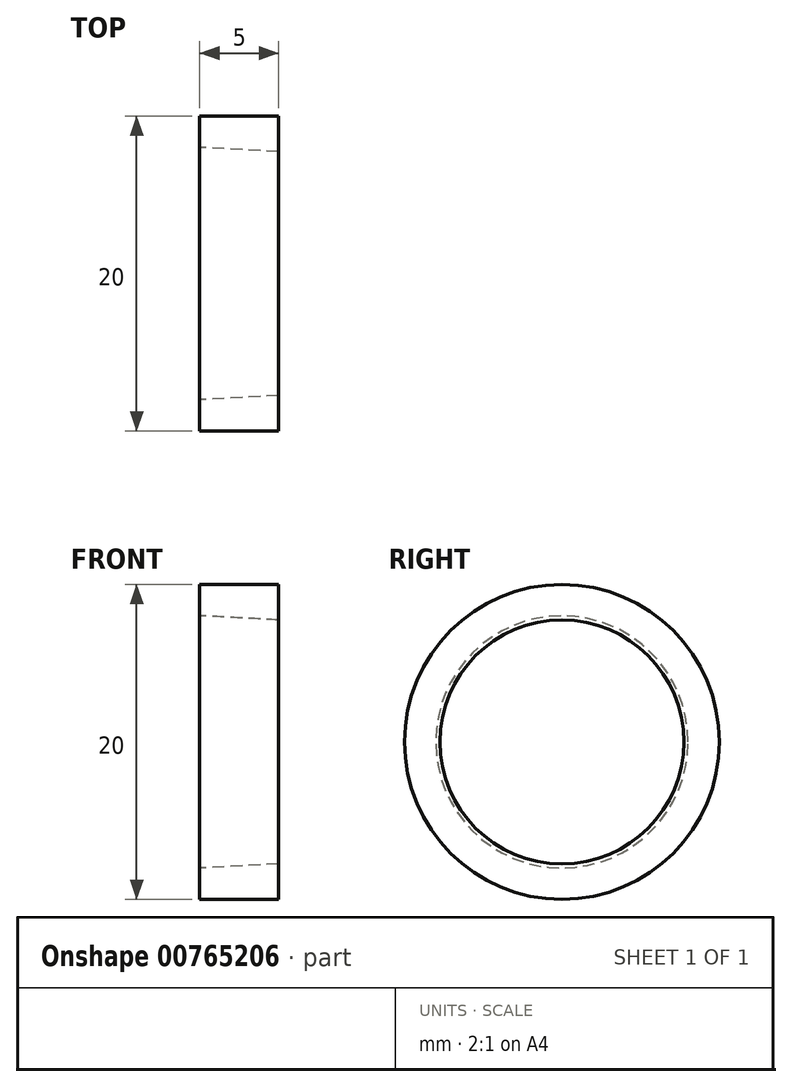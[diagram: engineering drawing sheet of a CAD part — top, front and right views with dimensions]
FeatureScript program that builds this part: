
annotation { "Feature Type Name" : "Feature", "Feature Type Description" : "" }
export const myFeature = defineFeature(function(context is Context, id is Id, definition is map)
    precondition{}
    {
        {
            var Q0;
            Q0=qCreatedBy(makeId("Front.planeOp"),FACE);
            var sketch = newSketch(context, id + "F0", { "sketchPlane" : qUnion([Q0])});
            skLineSegment(sketch, "E0", {"start": v(0, 10) * mm, "end": v(5, 10) * mm});
            skLineSegment(sketch, "E1", {"start": v(5, 7.75) * mm, "end": v(0, 8.01) * mm});
            skLineSegment(sketch, "E2", {"start": v(0, 8.01) * mm, "end": v(0, 10) * mm});
            skLineSegment(sketch, "E3", {"start": v(0, 0) * mm, "end": v(5, 0) * mm, "construction": true});
            skLineSegment(sketch, "E4", {"start": v(5, 7.75) * mm, "end": v(5, 10) * mm});
            skSolve(sketch);
        }
        {
            var Q0;
            Q0=makeQuery(id+"F0.imprint","IMPRINT",FACE,{"disambiguationData":[TD([[makeQuery(id+"F0.imprint","IMPRINT",EDGE,{"derivedFrom":sQuery(id+"F0.wireOp",EDGE,"E0")}),-1.0]])]});
            var Q1;
            Q1=sQuery(id+"F0.wireOp",EDGE,"E3");
            revolve(context, id + "F1", {"surfaceOperationType" : NewSurfaceOperationType.NEW, "entities" : qUnion([Q0]), "axis" : qUnion([Q1]), "revolveType" : RevolveType.FULL});
        }
    });
